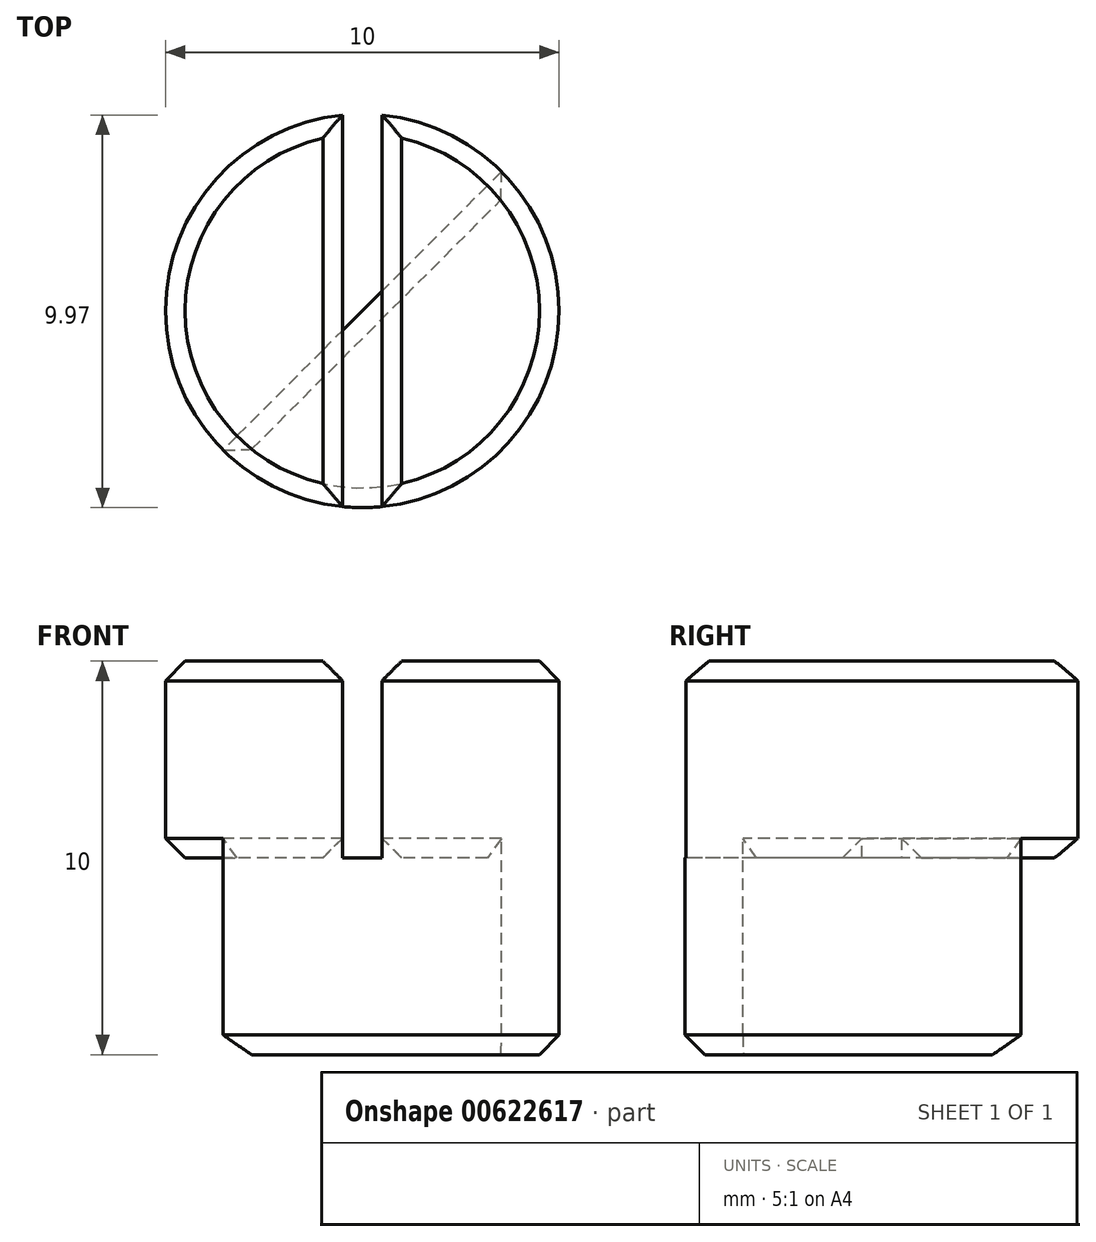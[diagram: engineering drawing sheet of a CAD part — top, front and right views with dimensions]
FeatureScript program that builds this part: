
annotation { "Feature Type Name" : "Feature", "Feature Type Description" : "" }
export const myFeature = defineFeature(function(context is Context, id is Id, definition is map)
    precondition{}
    {
        {
            var Q0;
            Q0=qCreatedBy(makeId("Top.planeOp"),FACE);
            var sketch = newSketch(context, id + "F0", { "sketchPlane" : qUnion([Q0])});
            skCircle(sketch, "E0", {"center": v(0, 0) * mm, "radius": 5 * mm});
            skLineSegment(sketch, "E1", {"start": v(0, 5) * mm, "end": v(0, -5) * mm});
            skArc(sketch, "E2.0.startCap", {"start": v(-0.5, 5) * mm, "mid": v(0, 5.5) * mm, "end": v(0.5, 5) * mm});
            skArc(sketch, "E2.0.endCap", {"start": v(0.5, -5) * mm, "mid": v(0, -5.5) * mm, "end": v(-0.5, -5) * mm});
            skLineSegment(sketch, "E2.0.left", {"start": v(0.5, 5) * mm, "end": v(0.5, -5) * mm});
            skLineSegment(sketch, "E2.0.right", {"start": v(-0.5, 5) * mm, "end": v(-0.5, -5) * mm});
            skLineSegment(sketch, "E3", {"start": v(3.54, 3.54) * mm, "end": v(-3.54, -3.54) * mm});
            skSolve(sketch);
        }
        {
            var Q0;
            {var subQ0=sQuery(id+"F0.wireOp",EDGE,"E3");var subQ1=sQuery(id+"F0.wireOp",EDGE,"E0");var subQ2=makeQuery(id+"F0.imprint","INTERSECT",VERTEX,{"disambiguationData":[OD(1.0)],"derivedFrom":[subQ1,subQ0]});Q0=makeQuery(id+"F0.imprint","IMPRINT",FACE,{"disambiguationData":[TD([[makeQuery(id+"F0.imprint","IMPRINT",EDGE,{"disambiguationData":[TD([[subQ2,-1.0]])],"derivedFrom":subQ1}),1.0]])]});}
            var Q1;
            {var subQ0=sQuery(id+"F0.wireOp",EDGE,"E1");var subQ1=sQuery(id+"F0.wireOp",EDGE,"E0");var subQ2=makeQuery(id+"F0.imprint","INTERSECT",VERTEX,{"disambiguationData":[OD(1.0)],"derivedFrom":[subQ1,subQ0]});Q1=makeQuery(id+"F0.imprint","IMPRINT",FACE,{"disambiguationData":[TD([[makeQuery(id+"F0.imprint","IMPRINT",EDGE,{"disambiguationData":[TD([[subQ2,1.0]])],"derivedFrom":subQ1}),1.0]])]});}
            var Q2;
            {var subQ0=sQuery(id+"F0.wireOp",EDGE,"E1");var subQ1=sQuery(id+"F0.wireOp",EDGE,"E0");var subQ2=makeQuery(id+"F0.imprint","INTERSECT",VERTEX,{"disambiguationData":[OD(1.0)],"derivedFrom":[subQ1,subQ0]});Q2=makeQuery(id+"F0.imprint","IMPRINT",FACE,{"disambiguationData":[TD([[makeQuery(id+"F0.imprint","IMPRINT",EDGE,{"disambiguationData":[TD([[subQ2,-1.0]])],"derivedFrom":subQ1}),1.0]])]});}
            var Q3;
            {var subQ0=sQuery(id+"F0.wireOp",EDGE,"E3");var subQ1=sQuery(id+"F0.wireOp",EDGE,"E0");var subQ2=makeQuery(id+"F0.imprint","INTERSECT",VERTEX,{"disambiguationData":[OD(0.0)],"derivedFrom":[subQ1,subQ0]});Q3=makeQuery(id+"F0.imprint","IMPRINT",FACE,{"disambiguationData":[TD([[makeQuery(id+"F0.imprint","IMPRINT",EDGE,{"disambiguationData":[TD([[subQ2,1.0]])],"derivedFrom":subQ1}),1.0]])]});}
            extrude(context, id + "F1", {"entities" : qUnion([Q0, Q1, Q2, Q3]), "oppositeDirection" : true, "depth" : 5 * mm, "offsetDistance" : 25 * mm});
        }
        {
            var Q0;
            {var subQ0=sQuery(id+"F0.wireOp",EDGE,"E3");var subQ1=sQuery(id+"F0.wireOp",EDGE,"E0");var subQ2=makeQuery(id+"F0.imprint","INTERSECT",VERTEX,{"disambiguationData":[OD(1.0)],"derivedFrom":[subQ1,subQ0]});Q0=makeQuery(id+"F0.imprint","IMPRINT",FACE,{"disambiguationData":[TD([[makeQuery(id+"F0.imprint","IMPRINT",EDGE,{"disambiguationData":[TD([[subQ2,1.0]])],"derivedFrom":subQ1}),1.0]])]});}
            var Q1;
            {var subQ0=sQuery(id+"F0.wireOp",EDGE,"E3");var subQ1=sQuery(id+"F0.wireOp",EDGE,"E0");var subQ2=makeQuery(id+"F0.imprint","INTERSECT",VERTEX,{"disambiguationData":[OD(0.0)],"derivedFrom":[subQ1,subQ0]});Q1=makeQuery(id+"F0.imprint","IMPRINT",FACE,{"disambiguationData":[TD([[makeQuery(id+"F0.imprint","IMPRINT",EDGE,{"disambiguationData":[TD([[subQ2,-1.0]])],"derivedFrom":subQ1}),1.0]])]});}
            var Q2;
            {var subQ0=sQuery(id+"F0.wireOp",EDGE,"E3");var subQ1=sQuery(id+"F0.wireOp",EDGE,"E0");var subQ2=makeQuery(id+"F0.imprint","INTERSECT",VERTEX,{"disambiguationData":[OD(0.0)],"derivedFrom":[subQ1,subQ0]});Q2=makeQuery(id+"F0.imprint","IMPRINT",FACE,{"disambiguationData":[TD([[makeQuery(id+"F0.imprint","IMPRINT",EDGE,{"disambiguationData":[TD([[subQ2,1.0]])],"derivedFrom":subQ1}),1.0]])]});}
            var Q3;
            {var subQ0=sQuery(id+"F0.wireOp",EDGE,"E3");var subQ1=sQuery(id+"F0.wireOp",EDGE,"E0");var subQ2=makeQuery(id+"F0.imprint","INTERSECT",VERTEX,{"disambiguationData":[OD(1.0)],"derivedFrom":[subQ1,subQ0]});Q3=makeQuery(id+"F0.imprint","IMPRINT",FACE,{"disambiguationData":[TD([[makeQuery(id+"F0.imprint","IMPRINT",EDGE,{"disambiguationData":[TD([[subQ2,-1.0]])],"derivedFrom":subQ1}),1.0]])]});}
            extrude(context, id + "F2", {"entities" : qUnion([Q0, Q1, Q2, Q3]), "operationType" : NewBodyOperationType.ADD, "depth" : 5 * mm, "offsetDistance" : 25 * mm});
        }
        {
            var Q0;
            Q0=makeQuery(id+"F2.opExtrude","CAP_FACE",FACE,{"disambiguationData":[OSD([sQuery(id+"F0.wireOp",EDGE,"E0"),sQuery(id+"F0.wireOp",EDGE,"E2.0.left")])],"isStart":false});
            var Q1;
            Q1=makeQuery(id+"F2.opExtrude","CAP_FACE",FACE,{"disambiguationData":[OSD([sQuery(id+"F0.wireOp",EDGE,"E0"),sQuery(id+"F0.wireOp",EDGE,"E2.0.right")])],"isStart":false});
            var Q2;
            Q2=makeQuery(id+"F1.opExtrude","CAP_FACE",FACE,{"disambiguationData":[OSD([sQuery(id+"F0.wireOp",EDGE,"E0"),sQuery(id+"F0.wireOp",EDGE,"E3")])],"isStart":false});
            var Q3;
            {var subQ0=sQuery(id+"F0.wireOp",EDGE,"E0");var subQ1=makeQuery(id+"F0.imprint","INTERSECT",VERTEX,{"disambiguationData":[OD(1.0)],"derivedFrom":[subQ0,sQuery(id+"F0.wireOp",EDGE,"E3")]});Q3=makeQuery(id+"F2.opExtrude","CAP_EDGE",EDGE,{"disambiguationData":[OSD([subQ0]),TDD([makeQuery(id+"F0.imprint","IMPRINT",EDGE,{"disambiguationData":[TD([[subQ1,1.0]])],"derivedFrom":subQ0}),makeQuery(id+"F0.imprint","IMPRINT",EDGE,{"disambiguationData":[TD([[subQ1,-1.0]])],"derivedFrom":subQ0})])],"isStart":true});}
            var Q4;
            {var subQ0=sQuery(id+"F0.wireOp",EDGE,"E0");var subQ1=makeQuery(id+"F0.imprint","INTERSECT",VERTEX,{"disambiguationData":[OD(0.0)],"derivedFrom":[subQ0,sQuery(id+"F0.wireOp",EDGE,"E3")]});Q4=makeQuery(id+"F2.opExtrude","CAP_EDGE",EDGE,{"disambiguationData":[OSD([subQ0]),TDD([makeQuery(id+"F0.imprint","IMPRINT",EDGE,{"disambiguationData":[TD([[subQ1,-1.0]])],"derivedFrom":subQ0}),makeQuery(id+"F0.imprint","IMPRINT",EDGE,{"disambiguationData":[TD([[subQ1,1.0]])],"derivedFrom":subQ0})])],"isStart":true});}
            var Q5;
            {var subQ0=sQuery(id+"F0.wireOp",EDGE,"E2.0.left");Q5=makeQuery(id+"F2.boolean.opBoolean","SPLIT",EDGE,{"disambiguationData":[topologyDisambiguationEdgeConnected([makeQuery(id+"F2.opExtrude","CAP_FACE",FACE,{"disambiguationData":[OSD([sQuery(id+"F0.wireOp",EDGE,"E0"),subQ0])],"isStart":true})])],"derivedFrom":makeQuery(id+"F2.opExtrude","CAP_EDGE",EDGE,{"disambiguationData":[OSD([subQ0])],"isStart":true})});}
            var Q6;
            {var subQ0=sQuery(id+"F0.wireOp",EDGE,"E2.0.right");Q6=makeQuery(id+"F2.boolean.opBoolean","SPLIT",EDGE,{"disambiguationData":[topologyDisambiguationEdgeConnected([makeQuery(id+"F2.opExtrude","CAP_FACE",FACE,{"disambiguationData":[OSD([sQuery(id+"F0.wireOp",EDGE,"E0"),subQ0])],"isStart":true})])],"derivedFrom":makeQuery(id+"F2.opExtrude","CAP_EDGE",EDGE,{"disambiguationData":[OSD([subQ0])],"isStart":true})});}
            chamfer(context, id + "F3", {"entities" : qUnion([Q0, Q1, Q2, Q3, Q4, Q5, Q6]), "width" : 0.5 * mm, "tangentPropagation" : true});
        }
    });
